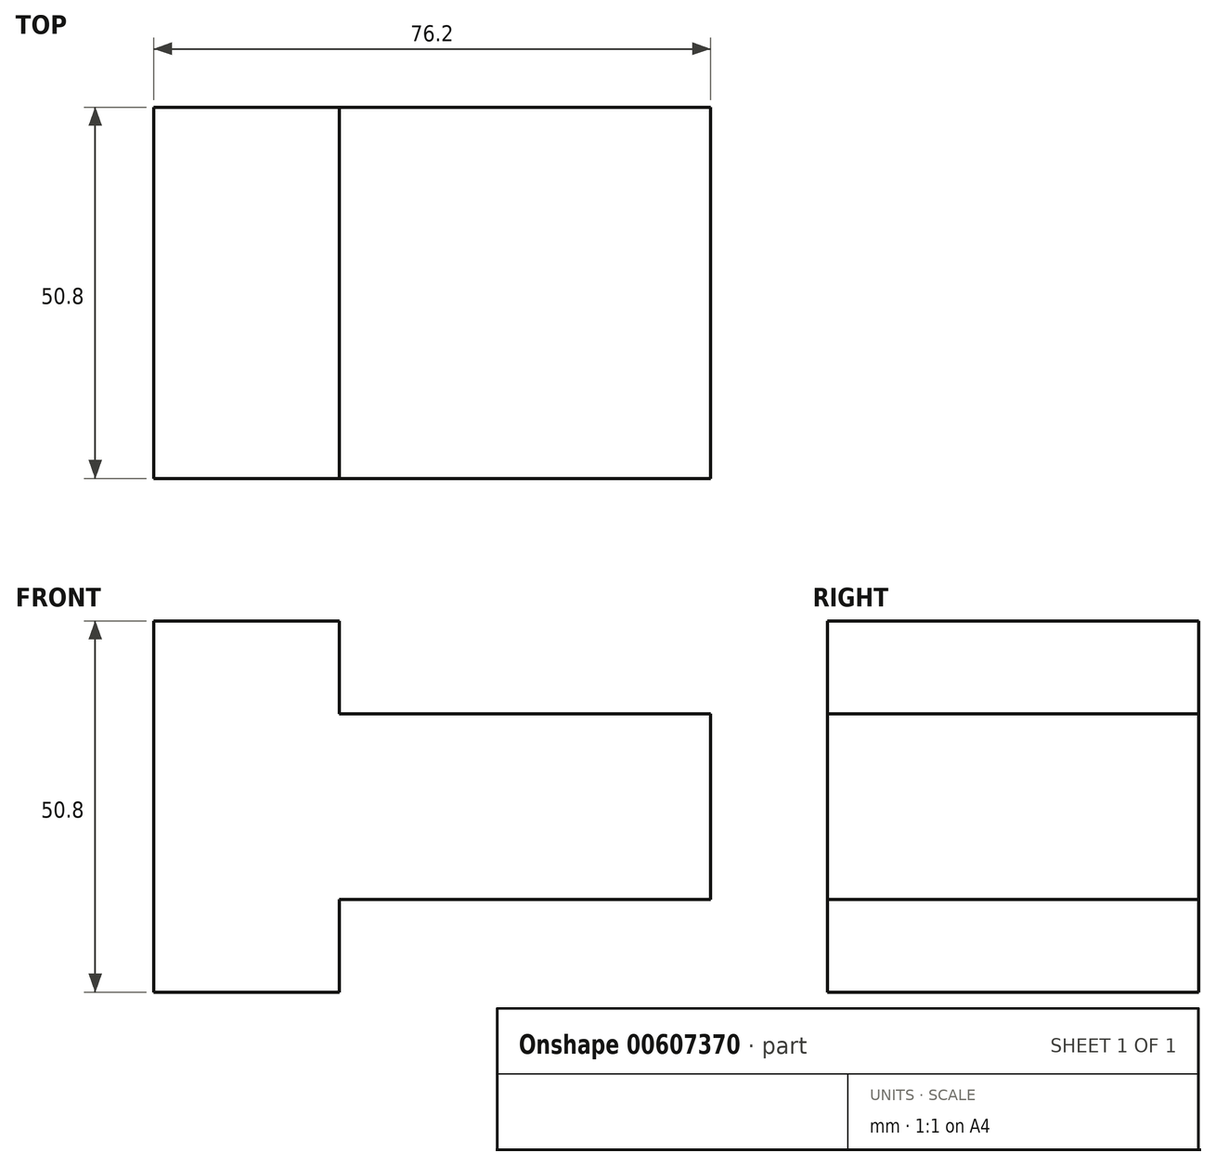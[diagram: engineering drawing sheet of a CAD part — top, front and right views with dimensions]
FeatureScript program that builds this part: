
annotation { "Feature Type Name" : "Feature", "Feature Type Description" : "" }
export const myFeature = defineFeature(function(context is Context, id is Id, definition is map)
    precondition{}
    {
        {
            var Q0;
            Q0=qCreatedBy(makeId("Front.planeOp"),FACE);
            var sketch = newSketch(context, id + "F0", { "sketchPlane" : qUnion([Q0])});
            skLineSegment(sketch, "E0", {"start": v(0, 0) * mm, "end": v(0, 50.8) * mm});
            skLineSegment(sketch, "E1", {"start": v(0, 50.8) * mm, "end": v(25.4, 50.8) * mm});
            skLineSegment(sketch, "E2", {"start": v(25.4, 50.8) * mm, "end": v(25.4, 38.1) * mm});
            skLineSegment(sketch, "E3", {"start": v(25.4, 38.1) * mm, "end": v(76.2, 38.1) * mm});
            skLineSegment(sketch, "E4", {"start": v(76.2, 38.1) * mm, "end": v(76.2, 12.7) * mm});
            skLineSegment(sketch, "E5", {"start": v(76.2, 12.7) * mm, "end": v(25.4, 12.7) * mm});
            skLineSegment(sketch, "E6", {"start": v(25.4, 12.7) * mm, "end": v(25.4, 0) * mm});
            skLineSegment(sketch, "E7", {"start": v(0, 0) * mm, "end": v(27.74, 0) * mm});
            skSolve(sketch);
        }
        {
            var Q0;
            {var subQ0=sQuery(id+"F0.wireOp",EDGE,"E0");Q0=makeQuery(id+"F0.imprint","IMPRINT",FACE,{"disambiguationData":[TD([[makeQuery(id+"F0.imprint","IMPRINT",EDGE,{"derivedFrom":subQ0}),-1.0]])]});}
            extrude(context, id + "F1", {"entities" : qUnion([Q0]), "depth" : 50.8 * mm, "offsetDistance" : 25.4 * mm});
        }
    });
